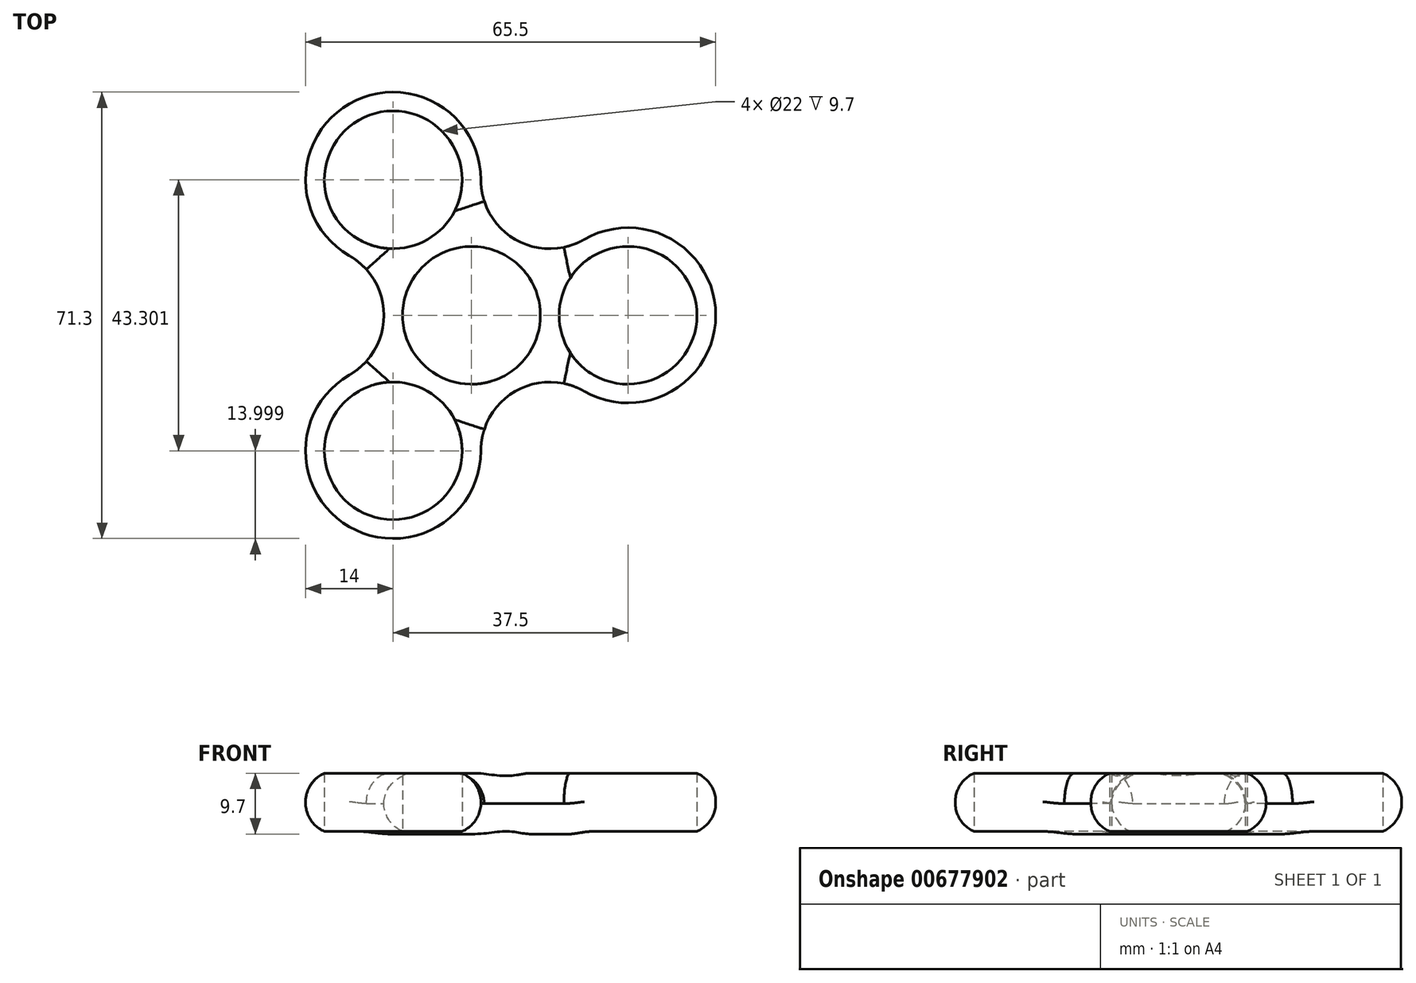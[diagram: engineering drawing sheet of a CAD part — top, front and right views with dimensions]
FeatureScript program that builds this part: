
annotation { "Feature Type Name" : "Feature", "Feature Type Description" : "" }
export const myFeature = defineFeature(function(context is Context, id is Id, definition is map)
    precondition{}
    {
        {
            var Q0;
            Q0=qCreatedBy(makeId("Top.planeOp"),FACE);
            var sketch = newSketch(context, id + "F0", { "sketchPlane" : qUnion([Q0])});
            skCircle(sketch, "E0", {"center": v(0, 0) * mm, "radius": 11 * mm});
            skCircle(sketch, "E1.2.0", {"center": v(-37.5, 21.65) * mm, "radius": 11 * mm});
            skPoint(sketch, "E1.center", {"position": v(-25, 0) * mm});
            skCircle(sketch, "E2.0.4.0", {"center": v(-37.5, -21.65) * mm, "radius": 11 * mm});
            skCircle(sketch, "E3", {"center": v(-25, 0) * mm, "radius": 11 * mm});
            skArc(sketch, "E4", {"start": v(-23.5, 21.65) * mm, "mid": v(-44.5, 33.77) * mm, "end": v(-44.5, 9.53) * mm});
            skArc(sketch, "E5", {"start": v(-44.5, -9.53) * mm, "mid": v(-44.5, -33.77) * mm, "end": v(-23.5, -21.65) * mm});
            skArc(sketch, "E6", {"start": v(-7, -12.12) * mm, "mid": v(14, 0) * mm, "end": v(-7, 12.12) * mm});
            skArc(sketch, "E7", {"start": v(-44.5, -9.53) * mm, "mid": v(-39, 0) * mm, "end": v(-44.5, 9.53) * mm});
            skArc(sketch, "E8", {"start": v(-23.5, 21.65) * mm, "mid": v(-18, 12.12) * mm, "end": v(-7, 12.12) * mm});
            skArc(sketch, "E9", {"start": v(-7, -12.12) * mm, "mid": v(-18, -12.12) * mm, "end": v(-23.5, -21.65) * mm});
            skLineSegment(sketch, "E10", {"start": v(-25, 0) * mm, "end": v(-12.5, 21.65) * mm, "construction": true});
            skLineSegment(sketch, "E11", {"start": v(-25, 0) * mm, "end": v(0, 0) * mm, "construction": true});
            skLineSegment(sketch, "E12", {"start": v(-25, 0) * mm, "end": v(-12.5, -21.65) * mm, "construction": true});
            skLineSegment(sketch, "E13", {"start": v(-25, 0) * mm, "end": v(-37.5, -21.65) * mm, "construction": true});
            skLineSegment(sketch, "E14", {"start": v(-25, 0) * mm, "end": v(-50, 0) * mm, "construction": true});
            skLineSegment(sketch, "E15", {"start": v(-25, 0) * mm, "end": v(-37.5, 21.65) * mm, "construction": true});
            skLineSegment(sketch, "E16.trimOffspring", {"start": v(-39, 0) * mm, "end": v(-39, 0) * mm});
            skSolve(sketch);
        }
        {
            var Q0;
            Q0=makeQuery(id+"F0.imprint","IMPRINT",FACE,{"disambiguationData":[TD([[makeQuery(id+"F0.imprint","IMPRINT",EDGE,{"derivedFrom":sQuery(id+"F0.wireOp",EDGE,"E0")}),-1.0]])]});
            extrude(context, id + "F1", {"entities" : qUnion([Q0]), "depth" : 9.7 * mm, "offsetDistance" : 25 * mm});
        }
        {
            var Q0;
            Q0=makeQuery(id+"F1.opExtrude","CAP_EDGE",EDGE,{"disambiguationData":[OSD([sQuery(id+"F0.wireOp",EDGE,"E5")])],"isStart":false});
            var Q1;
            Q1=makeQuery(id+"F1.opExtrude","CAP_EDGE",EDGE,{"disambiguationData":[OSD([sQuery(id+"F0.wireOp",EDGE,"E7")])],"isStart":false});
            var Q2;
            Q2=makeQuery(id+"F1.opExtrude","CAP_EDGE",EDGE,{"disambiguationData":[OSD([sQuery(id+"F0.wireOp",EDGE,"E4")])],"isStart":false});
            var Q3;
            Q3=makeQuery(id+"F1.opExtrude","CAP_EDGE",EDGE,{"disambiguationData":[OSD([sQuery(id+"F0.wireOp",EDGE,"E8")])],"isStart":false});
            var Q4;
            Q4=makeQuery(id+"F1.opExtrude","CAP_EDGE",EDGE,{"disambiguationData":[OSD([sQuery(id+"F0.wireOp",EDGE,"E6")])],"isStart":false});
            var Q5;
            Q5=makeQuery(id+"F1.opExtrude","CAP_EDGE",EDGE,{"disambiguationData":[OSD([sQuery(id+"F0.wireOp",EDGE,"E9")])],"isStart":false});
            fillet(context, id + "F2", {"entities" : qUnion([Q0, Q1, Q2, Q3, Q4, Q5]), "radius" : 5 * mm, "tangentPropagation" : true, "allowEdgeOverflow" : false});
        }
        {
            var Q0;
            Q0=makeQuery(id+"F1.opExtrude","CAP_EDGE",EDGE,{"disambiguationData":[OSD([sQuery(id+"F0.wireOp",EDGE,"E5")])],"isStart":true});
            var Q1;
            Q1=makeQuery(id+"F1.opExtrude","CAP_EDGE",EDGE,{"disambiguationData":[OSD([sQuery(id+"F0.wireOp",EDGE,"E7")])],"isStart":true});
            var Q2;
            Q2=makeQuery(id+"F1.opExtrude","CAP_EDGE",EDGE,{"disambiguationData":[OSD([sQuery(id+"F0.wireOp",EDGE,"E9")])],"isStart":true});
            var Q3;
            Q3=makeQuery(id+"F1.opExtrude","CAP_EDGE",EDGE,{"disambiguationData":[OSD([sQuery(id+"F0.wireOp",EDGE,"E6")])],"isStart":true});
            var Q4;
            Q4=makeQuery(id+"F1.opExtrude","CAP_EDGE",EDGE,{"disambiguationData":[OSD([sQuery(id+"F0.wireOp",EDGE,"E8")])],"isStart":true});
            var Q5;
            Q5=makeQuery(id+"F1.opExtrude","CAP_EDGE",EDGE,{"disambiguationData":[OSD([sQuery(id+"F0.wireOp",EDGE,"E4")])],"isStart":true});
            fillet(context, id + "F3", {"entities" : qUnion([Q0, Q1, Q2, Q3, Q4, Q5]), "radius" : 5 * mm, "tangentPropagation" : true, "allowEdgeOverflow" : false});
        }
    });
